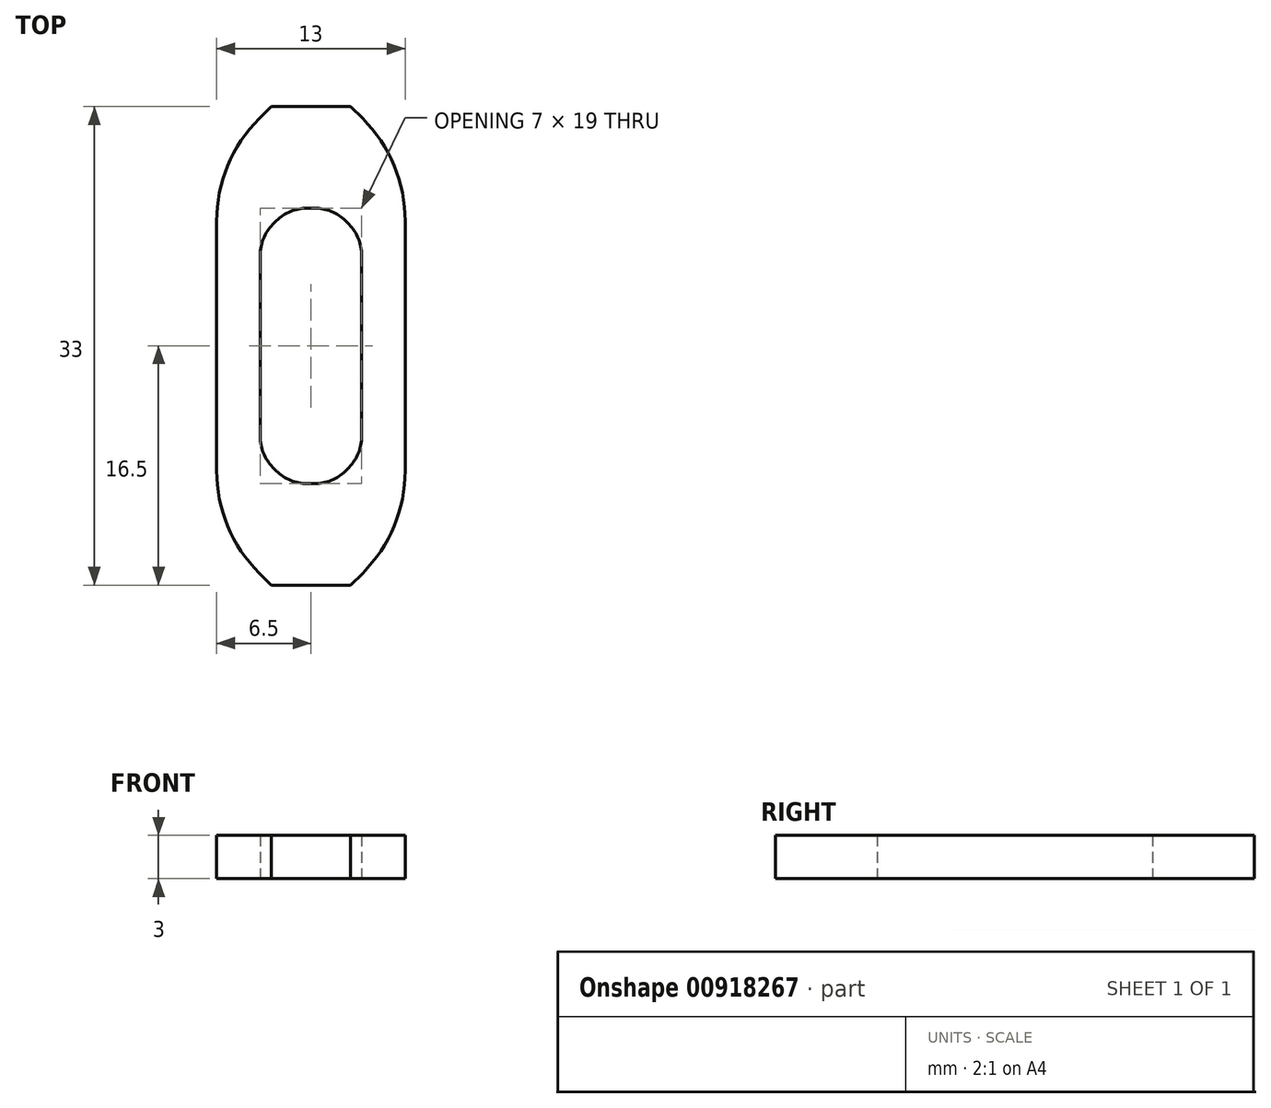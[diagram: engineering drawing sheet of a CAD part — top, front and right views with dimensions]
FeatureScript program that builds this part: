
annotation { "Feature Type Name" : "Feature", "Feature Type Description" : "" }
export const myFeature = defineFeature(function(context is Context, id is Id, definition is map)
    precondition{}
    {
        {
            var Q0;
            Q0=qCreatedBy(makeId("Top.planeOp"),FACE);
            var sketch = newSketch(context, id + "F0", { "sketchPlane" : qUnion([Q0])});
            skLineSegment(sketch, "E0.bottom", {"start": v(-1.5, 9.5) * mm, "end": v(1.5, 9.5) * mm});
            skLineSegment(sketch, "E0.top", {"start": v(-1.5, -9.5) * mm, "end": v(1.5, -9.5) * mm});
            skLineSegment(sketch, "E0.left", {"start": v(-3.5, 7.5) * mm, "end": v(-3.5, -7.5) * mm});
            skLineSegment(sketch, "E0.right", {"start": v(3.5, 7.5) * mm, "end": v(3.5, -7.5) * mm});
            skPoint(sketch, "E0.middle", {"position": v(0, 0) * mm});
            skLineSegment(sketch, "E1", {"start": v(-3.5, 7.5) * mm, "end": v(-1.5, 9.5) * mm});
            skLineSegment(sketch, "E2", {"start": v(-3.5, 0) * mm, "end": v(3.5, 0) * mm, "construction": true});
            skLineSegment(sketch, "E3", {"start": v(0, 9.5) * mm, "end": v(0, -9.5) * mm, "construction": true});
            skLineSegment(sketch, "E4.MirrorCS", {"start": v(3.5, 7.5) * mm, "end": v(1.5, 9.5) * mm});
            skLineSegment(sketch, "E5.MirrorCS", {"start": v(-3.5, -7.5) * mm, "end": v(-1.5, -9.5) * mm});
            skLineSegment(sketch, "E6.MirrorCS", {"start": v(3.5, -7.5) * mm, "end": v(1.5, -9.5) * mm});
            skPoint(sketch, "E7.orphan", {"position": v(3.5, 9.5) * mm});
            skPoint(sketch, "E8.orphan", {"position": v(3.5, -9.5) * mm});
            skPoint(sketch, "E9.orphan", {"position": v(-3.5, -9.5) * mm});
            skPoint(sketch, "E10.orphan", {"position": v(-3.5, 9.5) * mm});
            skLineSegment(sketch, "E11.0", {"start": v(-6.5, 8.74) * mm, "end": v(-2.74, 12.5) * mm, "construction": true});
            skLineSegment(sketch, "E11.1", {"start": v(-6.5, 8.74) * mm, "end": v(-6.5, -8.74) * mm});
            skLineSegment(sketch, "E11.2", {"start": v(-2.74, 12.5) * mm, "end": v(2.74, 12.5) * mm, "construction": true});
            skLineSegment(sketch, "E11.3", {"start": v(-6.5, -8.74) * mm, "end": v(-2.74, -12.5) * mm, "construction": true});
            skLineSegment(sketch, "E11.4", {"start": v(6.5, 8.74) * mm, "end": v(2.74, 12.5) * mm, "construction": true});
            skLineSegment(sketch, "E11.5", {"start": v(6.5, 8.74) * mm, "end": v(6.5, -8.74) * mm});
            skLineSegment(sketch, "E11.6", {"start": v(6.5, -8.74) * mm, "end": v(2.74, -12.5) * mm, "construction": true});
            skLineSegment(sketch, "E11.7", {"start": v(-2.74, -12.5) * mm, "end": v(2.74, -12.5) * mm});
            skLineSegment(sketch, "E12", {"start": v(-6.5, 8.74) * mm, "end": v(-6.5, 12.74) * mm});
            skLineSegment(sketch, "E13", {"start": v(-6.5, 12.74) * mm, "end": v(-2.74, 16.5) * mm});
            skLineSegment(sketch, "E14", {"start": v(-2.74, 16.5) * mm, "end": v(0, 16.5) * mm});
            skLineSegment(sketch, "E15.MirrorCS", {"start": v(2.74, 16.5) * mm, "end": v(0, 16.5) * mm});
            skLineSegment(sketch, "E16.MirrorCS", {"start": v(6.5, 12.74) * mm, "end": v(2.74, 16.5) * mm});
            skLineSegment(sketch, "E17.MirrorCS", {"start": v(6.5, 8.74) * mm, "end": v(6.5, 12.74) * mm});
            skLineSegment(sketch, "E18.MirrorCS", {"start": v(6.5, -8.74) * mm, "end": v(6.5, -12.74) * mm});
            skLineSegment(sketch, "E19.MirrorCS", {"start": v(6.5, -12.74) * mm, "end": v(2.74, -16.5) * mm});
            skLineSegment(sketch, "E20.MirrorCS", {"start": v(2.74, -16.5) * mm, "end": v(0, -16.5) * mm});
            skLineSegment(sketch, "E21.MirrorCS", {"start": v(-2.74, -16.5) * mm, "end": v(0, -16.5) * mm});
            skLineSegment(sketch, "E22.MirrorCS", {"start": v(-6.5, -12.74) * mm, "end": v(-2.74, -16.5) * mm});
            skLineSegment(sketch, "E23.MirrorCS", {"start": v(-6.5, -8.74) * mm, "end": v(-6.5, -12.74) * mm});
            skLineSegment(sketch, "E24.MirrorCS", {"start": v(-6.5, -8.74) * mm, "end": v(-2.74, -12.5) * mm});
            skLineSegment(sketch, "E25.MirrorCS", {"start": v(-2.74, -12.5) * mm, "end": v(2.74, -12.5) * mm, "construction": true});
            skSolve(sketch);
        }
        {
            var Q0;
            Q0=qSketchRegion(id+"F0",true);
            extrude(context, id + "F1", {"entities" : qUnion([Q0]), "depth" : 3 * mm});
        }
        {
            var Q0;
            Q0=makeQuery(id+"F1.opExtrude","SWEPT_EDGE",EDGE,{"disambiguationData":[OSD([sQuery(id+"F0.wireOp",EDGE,"E0.left"),sQuery(id+"F0.wireOp",EDGE,"E1")])]});
            var Q1;
            Q1=makeQuery(id+"F1.opExtrude","SWEPT_EDGE",EDGE,{"disambiguationData":[OSD([sQuery(id+"F0.wireOp",EDGE,"E0.right"),sQuery(id+"F0.wireOp",EDGE,"E4.MirrorCS")])]});
            var Q2;
            Q2=makeQuery(id+"F1.opExtrude","SWEPT_EDGE",EDGE,{"disambiguationData":[OSD([sQuery(id+"F0.wireOp",EDGE,"E0.right"),sQuery(id+"F0.wireOp",EDGE,"E6.MirrorCS")])]});
            var Q3;
            Q3=makeQuery(id+"F1.opExtrude","SWEPT_EDGE",EDGE,{"disambiguationData":[OSD([sQuery(id+"F0.wireOp",EDGE,"E0.left"),sQuery(id+"F0.wireOp",EDGE,"E5.MirrorCS")])]});
            var Q4;
            Q4=makeQuery(id+"F1.opExtrude","SWEPT_EDGE",EDGE,{"disambiguationData":[OSD([sQuery(id+"F0.wireOp",EDGE,"E0.bottom"),sQuery(id+"F0.wireOp",EDGE,"E1")])]});
            var Q5;
            Q5=makeQuery(id+"F1.opExtrude","SWEPT_EDGE",EDGE,{"disambiguationData":[OSD([sQuery(id+"F0.wireOp",EDGE,"E0.bottom"),sQuery(id+"F0.wireOp",EDGE,"E4.MirrorCS")])]});
            var Q6;
            Q6=makeQuery(id+"F1.opExtrude","SWEPT_EDGE",EDGE,{"disambiguationData":[OSD([sQuery(id+"F0.wireOp",EDGE,"E0.top"),sQuery(id+"F0.wireOp",EDGE,"E6.MirrorCS")])]});
            var Q7;
            Q7=makeQuery(id+"F1.opExtrude","SWEPT_EDGE",EDGE,{"disambiguationData":[OSD([sQuery(id+"F0.wireOp",EDGE,"E0.top"),sQuery(id+"F0.wireOp",EDGE,"E5.MirrorCS")])]});
            fillet(context, id + "F2", {"entities" : qUnion([Q0, Q1, Q2, Q3, Q4, Q5, Q6, Q7]), "radius" : 3 * mm, "tangentPropagation" : true, "allowEdgeOverflow" : false});
        }
        {
            var Q0;
            Q0=makeQuery(id+"F1.opExtrude","SWEPT_EDGE",EDGE,{"disambiguationData":[OSD([sQuery(id+"F0.wireOp",EDGE,"E12"),sQuery(id+"F0.wireOp",EDGE,"E13")])]});
            var Q1;
            Q1=makeQuery(id+"F1.opExtrude","SWEPT_EDGE",EDGE,{"disambiguationData":[OSD([sQuery(id+"F0.wireOp",EDGE,"E16.MirrorCS"),sQuery(id+"F0.wireOp",EDGE,"E17.MirrorCS")])]});
            var Q2;
            Q2=makeQuery(id+"F1.opExtrude","SWEPT_EDGE",EDGE,{"disambiguationData":[OSD([sQuery(id+"F0.wireOp",EDGE,"E18.MirrorCS"),sQuery(id+"F0.wireOp",EDGE,"E19.MirrorCS")])]});
            var Q3;
            Q3=makeQuery(id+"F1.opExtrude","SWEPT_EDGE",EDGE,{"disambiguationData":[OSD([sQuery(id+"F0.wireOp",EDGE,"E22.MirrorCS"),sQuery(id+"F0.wireOp",EDGE,"E23.MirrorCS")])]});
            fillet(context, id + "F3", {"entities" : qUnion([Q0, Q1, Q2, Q3]), "radius" : 10 * mm, "tangentPropagation" : true, "allowEdgeOverflow" : false});
        }
    });
